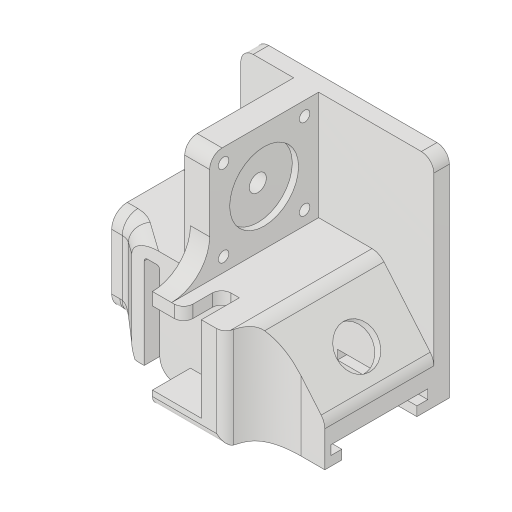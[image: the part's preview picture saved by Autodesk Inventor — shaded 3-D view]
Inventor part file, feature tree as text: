
AUTODESK INVENTOR PART (.ipt)
format: ipt  version: 2023.3 (Build 273359000, 359)  size: 974,336 bytes
history: native  units: in
note: dims shown in document units (in); Inventor stores cm internally (conversion verified against a paired STEP export)
features: sketch x20, extrude x12, fillet x10, hole x8, loft x3, plane x2, chamfer x2, sweep x1, projected_geometry x1
ambient origin geometry x8: Origin, YZ Plane, XZ Plane, XY Plane, X Axis, Y Axis, Z Axis, Center Point
bodies: Body1 (feature_tree)
feature tree (59):
  sketch  "Skizze3"  dims[d4=2.7165in d7=0.8701in]
  extrude  "Extrusion3"  Depth=0.8701in
  extrude  "Extrusion4"  Depth=0.3937in
  sketch  "Skizze47"  dims[d457=0.2559in d459=0.2362in]
  hole  "Bohrung19"  [1 undecoded]
  extrude  "Extrusion5"  Depth=1.378in TaperAngle=0.0deg
  sketch  "Skizze29"  dims[d10=0.8933in d12=0.1969in]
  hole  "Bohrung9"  [1 undecoded]
  hole  "Bohrung10"  [1 undecoded]
  extrude  "Extrusion27"  Depth=0.2559in
  hole  "Bohrung24"  [1 undecoded]
  fillet  "Rundung16"  Radius=0.315in
  sketch  "Skizze30"  dims[d16=2.4409in d18=1.378in d19=0.0in]
  plane  "Arbeitsebene11"
  sketch  "Skizze33"  dims[d38=0.0984in d88=0.2835in]
  extrude  "Extrusion28"  Depth=1.0236in
  sweep  "Sweeping3"
  fillet  "Rundung17"  Radius=0.3937in
  fillet  "Rundung18"  Radius=0.1969in
  fillet  "Rundung19"  Radius=0.1575in
  hole  "Bohrung12"  [1 undecoded]
  extrude  "Extrusion29"  Depth=0.1374in
  hole  "Bohrung14"  [1 undecoded]
  extrude  "Extrusion30"  Depth=0.1181in
  fillet  "Rundung21"  Radius=0.4724in
  sketch  "Skizze40"  dims[d426=0.2165in d427=0.2362in d428=0.1575in d429=0.0787in d430=90.0deg d431=0.1969in d432=0.0in]
  plane  "Arbeitsebene12"
  sketch  "Skizze41"  dims[d433=0.1339in d434=0.2362in d435=0.2559in d436=0.1339in d437=0.5635in d438=0.315in d439=0.0in d441=0.4724in d442=0.3937in d450=0.1969in d451=0.0in d452=0.1575in]
  extrude  "Extrusion31"  Depth=0.2362in
  loft  "Erhebung18"
  loft  "Erhebung20"
  loft  "Erhebung21"
  chamfer  "Fase3"  Distance=0.8701in
  extrude  "Extrusion33"  Depth=0.3937in TaperAngle=0.0deg
  fillet  "Rundung22"  Radius=1.0896in
  hole  "Bohrung17"  [1 undecoded]
  fillet  "Rundung23"  Radius=0.5906in
  fillet  "Rundung25"  [1 undecoded]
  extrude  "Extrusion36"  Depth=0.3937in
  fillet  "Rundung26"  Radius=0.315in
  fillet  "Rundung27"  Radius=0.1969in
  hole  "Bohrung20"  [1 undecoded]
  extrude  "Extrusion37"  Depth=0.3937in TaperAngle=0.0deg
  extrude  "Extrusion38"  Depth=0.3937in
  sketch  "Skizze53"  dims[d476=0.1181in d477=0.2362in d478=0.1575in d479=0.0787in d480=90.0deg d481=0.2756in d482=0.0in d483=0.8701in d484=0.0787in d485=0.0in d500=1.0896in d501=0.2362in d502=0.5118in d503=0.6299in d504=0.1575in d505=0.0787in d506=90.0deg d507=0.315in d508=0.8108in d509=0.5906in d510=90.0deg d512=0.1575in d513=0.315in d514=0.1969in d516=1.378in d517=0.315in d518=0.0in d519=0.0394in d533=0.0197in d534=0.9449in d535=0.9449in d537=0.1969in d538=0.9449in d539=0.6299in d540=0.7874in d541=0.7874in d542=1.1024in d543=1.1024in d546=0.1969in d547=0.0in d556=0.0in d557=90.0deg d558=0.0in d559=90.0deg d566=0.1575in d567=0.1181in d568=0.0787in d569=0.3937in d570=0.1181in d571=0.3937in d572=0.1575in d573=0.0in d574=90.0deg d575=0.0in d576=90.0deg d577=0.0in d578=90.0deg d581=0.1575in d582=0.0787in d583=0.0in d584=90.0deg d585=0.0787in d586=0.2165in d587=45.0deg d588=0.1969in d589=0.0in d590=0.1969in d604=0.0617in d605=0.1575in d606=0.1575in d607=0.0787in d608=90.0deg d609=0.248in d610=0.0in d624=0.1969in d626=0.0394in d629=0.1339in d630=0.2362in d631=0.2559in d632=0.1339in d633=90.0deg d634=0.3465in d635=0.0in d636=0.5846in d638=0.1575in d639=0.4803in d640=0.0in d641=0.9213in d642=0.189in d643=0.6181in d644=0.4803in d645=0.1181in d646=1.0945in d647=0.0846in d648=0.0669in d649=0.2362in d650=0.2559in d651=0.1339in d652=90.0deg d653=0.3465in d654=0.0in d655=0.3937in d657=0.1378in d658=0.5512in d683=0.2756in d684=0.1339in d685=0.2362in d686=0.2559in d687=0.1339in d688=90.0deg d689=0.7874in d690=0.0in d691=0.1969in d692=0.1457in d693=0.2165in d694=0.3937in d695=0.2756in d696=0.5413in d697=0.1378in d698=0.1181in d699=0.1181in d700=1.0039in d701=0.0in d702=0.0433in d703=1.0039in d704=0.0in d705=0.3937in d706=0.3937in d707=0.5906in d708=0.5906in d709=0.0591in d710=0.0787in d711=45.0deg d98=0.0197in d99=0.0344in d100=0.0197in d104=0.0197in d105=0.0344in d106=0.0197in d107=0.0344in d108=0.0344in d265=0.0197in d266=0.0344in d267=0.0197in d268=0.0344in d418=0.0197in d419=0.0344in d420=0.0197in d421=0.0344in d496=0.0197in d497=0.0344in d498=0.0197in d499=0.0344in]
  chamfer  "Fase4"  Distance=0.0197in
  sketch  "Skizze4"  dims[d8=0.8661in d9=0.3937in]
  sketch  "Skizze32"  dims[d20=0.9488in d21=0.0in d29=0.0in d30=0.0in]
  sketch  "Skizze34"  dims[d101=0.2559in d102=0.2559in]
  sketch  "Skizze36"  dims[d308=0.4114in d309=0.0in d364=0.0197in d423=0.315in]
  sketch  "Skizze37"  dims[d424=1.0236in d425=1.0236in]
  sketch  "Skizze43"  dims[d453=0.3937in d454=0.4724in]
  sketch  "Skizze44"  dims[d455=0.4331in d456=0.1374in]
  projected_geometry  "Projizierte Kontur18"
  sketch  "Skizze48"  dims[d461=0.3543in d462=0.1181in d465=0.4724in]
  sketch  "Skizze49"  dims[d466=0.2362in d467=0.2362in]
  sketch  "Skizze50"  dims[d468=0.1575in d469=0.0in d470=0.0689in]
  sketch  "Skizze51"  dims[d471=0.0in d472=0.0in d473=0.2362in]
  sketch  "Skizze52"  dims[d474=0.0787in d475=0.0354in]
note: 9 required parameter values undecoded (feature->parameter linkage not recoverable at this tier; creation-order binding heuristic only, values carry confidence <= 0.55)
